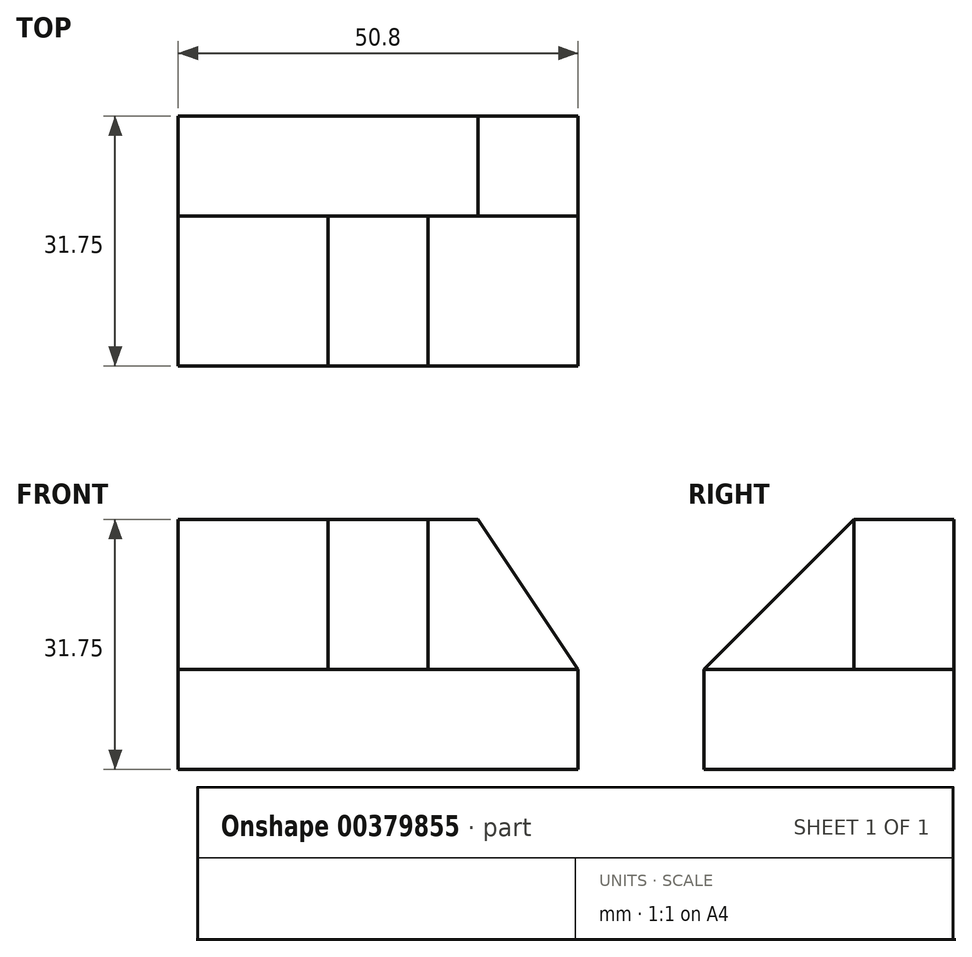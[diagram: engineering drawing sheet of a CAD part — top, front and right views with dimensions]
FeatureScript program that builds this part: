
annotation { "Feature Type Name" : "Feature", "Feature Type Description" : "" }
export const myFeature = defineFeature(function(context is Context, id is Id, definition is map)
    precondition{}
    {
        {
            var Q0;
            Q0=qCreatedBy(makeId("Right.planeOp"),FACE);
            var sketch = newSketch(context, id + "F0", { "sketchPlane" : qUnion([Q0])});
            skLineSegment(sketch, "E0", {"start": v(0, 0) * mm, "end": v(31.75, 0) * mm});
            skLineSegment(sketch, "E1", {"start": v(31.75, 0) * mm, "end": v(31.75, 31.75) * mm});
            skLineSegment(sketch, "E2", {"start": v(31.75, 31.75) * mm, "end": v(19.05, 31.75) * mm});
            skLineSegment(sketch, "E3", {"start": v(19.05, 31.75) * mm, "end": v(19.05, 12.7) * mm});
            skLineSegment(sketch, "E4", {"start": v(19.05, 12.7) * mm, "end": v(0, 12.7) * mm});
            skLineSegment(sketch, "E5", {"start": v(0, 0) * mm, "end": v(0, 12.7) * mm});
            skSolve(sketch);
        }
        {
            var Q0;
            Q0 = qSketchRegion(id + "F0", true);
            extrude(context, id + "F1", {"entities" : qUnion([Q0]), "depth" : 50.8 * mm});
        }
        {
            var Q0;
            Q0=makeQuery(id+"F1.opExtrude","SWEPT_FACE",FACE,{"disambiguationData":[OSD([sQuery(id+"F0.wireOp",EDGE,"E3")])]});
            var sketch = newSketch(context, id + "F2", { "sketchPlane" : qUnion([Q0])});
            skLineSegment(sketch, "E6", {"start": v(0, 31.75) * mm, "end": v(38.1, 31.75) * mm});
            skLineSegment(sketch, "E7", {"start": v(38.1, 31.75) * mm, "end": v(50.8, 12.7) * mm});
            skSolve(sketch);
        }
        {
            var Q0;
            Q0 = qSketchRegion(id + "F2", true);
            var Q1;
            {var subQ0=sQuery(id+"F2.wireOp",EDGE,"E7");Q1=makeQuery(id+"F2.imprint","IMPRINT",FACE,{"disambiguationData":[TD([[makeQuery(id+"F2.imprint","IMPRINT",EDGE,{"derivedFrom":subQ0}),1.0]])]});}
            extrude(context, id + "F3", {"entities" : qUnion([Q0, Q1]), "operationType" : NewBodyOperationType.REMOVE, "oppositeDirection" : true, "depth" : 25.4 * mm});
        }
        {
            var Q0;
            Q0=makeQuery(id+"F1.opExtrude","SWEPT_FACE",FACE,{"disambiguationData":[OSD([sQuery(id+"F0.wireOp",EDGE,"E3")])]});
            var sketch = newSketch(context, id + "F4", { "sketchPlane" : qUnion([Q0])});
            skLineSegment(sketch, "E8", {"start": v(0, 31.75) * mm, "end": v(19.05, 31.75) * mm});
            skLineSegment(sketch, "E9", {"start": v(19.05, 31.75) * mm, "end": v(19.05, 12.7) * mm});
            skLineSegment(sketch, "E10", {"start": v(19.05, 12.7) * mm, "end": v(31.75, 12.7) * mm});
            skLineSegment(sketch, "E11", {"start": v(31.75, 12.7) * mm, "end": v(31.75, 31.75) * mm});
            skSolve(sketch);
        }
        {
            var Q0;
            Q0 = qSketchRegion(id + "F4", true);
            var Q1;
            {var subQ0=sQuery(id+"F4.wireOp",EDGE,"E9");Q1=makeQuery(id+"F4.imprint","IMPRINT",FACE,{"disambiguationData":[TD([[makeQuery(id+"F4.imprint","IMPRINT",EDGE,{"derivedFrom":subQ0}),1.0]])]});}
            extrude(context, id + "F5", {"entities" : qUnion([Q0, Q1]), "operationType" : NewBodyOperationType.ADD, "depth" : 19.05 * mm});
        }
        {
            var Q0;
            Q0=makeQuery(id+"F5.opExtrude","SWEPT_FACE",FACE,{"disambiguationData":[OSD([sQuery(id+"F4.wireOp",EDGE,"E11")])]});
            var sketch = newSketch(context, id + "F6", { "sketchPlane" : qUnion([Q0])});
            skLineSegment(sketch, "E12", {"start": v(0, 12.7) * mm, "end": v(19.05, 31.75) * mm});
            skSolve(sketch);
        }
        {
            var Q0;
            Q0 = qSketchRegion(id + "F6", true);
            var Q1;
            Q1=makeQuery(id+"F6.imprint","IMPRINT",FACE,{"disambiguationData":[TD([[makeQuery(id+"F6.imprint","IMPRINT",EDGE,{"derivedFrom":sQuery(id+"F6.wireOp",EDGE,"E12")}),1.0]])]});
            extrude(context, id + "F7", {"entities" : qUnion([Q0, Q1]), "operationType" : NewBodyOperationType.REMOVE, "oppositeDirection" : true, "depth" : 25.4 * mm});
        }
    });
